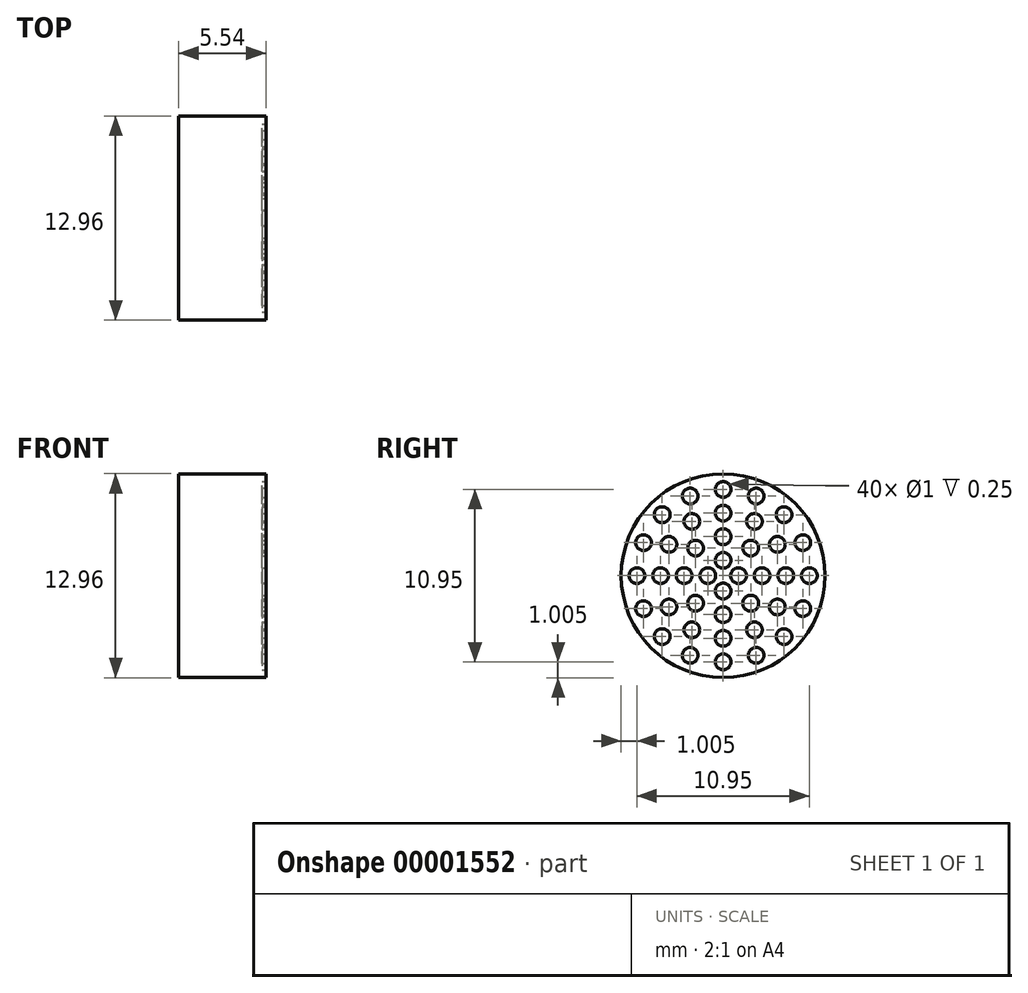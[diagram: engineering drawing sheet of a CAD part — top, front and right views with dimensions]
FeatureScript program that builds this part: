
annotation { "Feature Type Name" : "Feature", "Feature Type Description" : "" }
export const myFeature = defineFeature(function(context is Context, id is Id, definition is map)
    precondition{}
    {
        {
            var Q0;
            Q0=qCreatedBy(makeId("Right.planeOp"),FACE);
            var sketch = newSketch(context, id + "F0", { "sketchPlane" : qUnion([Q0])});
            skCircle(sketch, "E0", {"center": v(0, 0) * mm, "radius": 6.48 * mm});
            skSolve(sketch);
        }
        {
            var Q0;
            Q0 = qSketchRegion(id + "F0", true);
            extrude(context, id + "F1", {"entities" : qUnion([Q0]), "depth" : 5.54 * mm});
        }
        {
            var Q0;
            Q0=makeQuery(id+"F1.opExtrude","CAP_FACE",FACE,{"disambiguationData":[OSD([sQuery(id+"F0.wireOp",EDGE,"E0")])],"isStart":false});
            var sketch = newSketch(context, id + "F2", { "sketchPlane" : qUnion([Q0])});
            skCircle(sketch, "E1", {"center": v(0, 0) * mm, "radius": 5.48 * mm, "construction": true});
            skCircle(sketch, "E2", {"center": v(0, 5.48) * mm, "radius": 0.5 * mm});
            skCircle(sketch, "E3.0", {"center": v(0, 0) * mm, "radius": 3.98 * mm, "construction": true});
            skCircle(sketch, "E4", {"center": v(0, 0) * mm, "radius": 2.48 * mm, "construction": true});
            skCircle(sketch, "E5", {"center": v(0, 0) * mm, "radius": 0.98 * mm, "construction": true});
            skCircle(sketch, "E6", {"center": v(0, 3.98) * mm, "radius": 0.5 * mm});
            skCircle(sketch, "E7", {"center": v(0, 2.48) * mm, "radius": 0.5 * mm});
            skCircle(sketch, "E8", {"center": v(0, 0.98) * mm, "radius": 0.5 * mm});
            skSolve(sketch);
        }
        {
            var Q0;
            Q0=makeQuery(id+"F2.imprint","IMPRINT",FACE,{"disambiguationData":[TD([[makeQuery(id+"F2.imprint","IMPRINT",EDGE,{"derivedFrom":sQuery(id+"F2.wireOp",EDGE,"E2")}),1.0]])]});
            extrude(context, id + "F3", {"entities" : qUnion([Q0]), "operationType" : NewBodyOperationType.REMOVE, "oppositeDirection" : true, "depth" : .25 * mm});
        }
        {
            var Q0;
            Q0=makeQuery(id+"F3.boolean.opBoolean","COPY",FACE,{"derivedFrom":makeQuery(id+"F3.opExtrude","SWEPT_FACE",FACE,{"disambiguationData":[OSD([sQuery(id+"F2.wireOp",EDGE,"E2")])]})});
            var Q1;
            Q1=makeQuery(id+"F3.boolean.opBoolean","COPY",FACE,{"derivedFrom":makeQuery(id+"F3.opExtrude","CAP_FACE",FACE,{"disambiguationData":[OSD([sQuery(id+"F2.wireOp",EDGE,"E2")])],"isStart":false})});
            var Q2;
            Q2=sQuery(id+"F2.wireOp",EDGE,"E1");
            circularPattern(context, id + "F4", {"faces" : qUnion([Q0, Q1]), "axis" : qUnion([Q2]), "angle" : 360 * degree, "instanceCount" : 16, "equalSpace" : true, "patternType" : PatternType.FACE});
        }
        {
            var Q0;
            Q0=makeQuery(id+"F2.imprint","IMPRINT",FACE,{"disambiguationData":[TD([[makeQuery(id+"F2.imprint","IMPRINT",EDGE,{"derivedFrom":sQuery(id+"F2.wireOp",EDGE,"E6")}),1.0]])]});
            var Q1;
            Q1=sQuery(id+"F2.wireOp",EDGE,"E6");
            extrude(context, id + "F5", {"entities" : qUnion([Q0]), "operationType" : NewBodyOperationType.REMOVE, "surfaceEntities" : qUnion([Q1]), "oppositeDirection" : true, "depth" : .25 * mm});
        }
        {
            var Q0;
            Q0=makeQuery(id+"F2.imprint","IMPRINT",FACE,{"disambiguationData":[TD([[makeQuery(id+"F2.imprint","IMPRINT",EDGE,{"derivedFrom":sQuery(id+"F2.wireOp",EDGE,"E7")}),1.0]])]});
            extrude(context, id + "F6", {"entities" : qUnion([Q0]), "operationType" : NewBodyOperationType.REMOVE, "oppositeDirection" : true, "depth" : .25 * mm});
        }
        {
            var Q0;
            Q0=makeQuery(id+"F2.imprint","IMPRINT",FACE,{"disambiguationData":[TD([[makeQuery(id+"F2.imprint","IMPRINT",EDGE,{"derivedFrom":sQuery(id+"F2.wireOp",EDGE,"E8")}),1.0]])]});
            extrude(context, id + "F7", {"entities" : qUnion([Q0]), "operationType" : NewBodyOperationType.REMOVE, "oppositeDirection" : true, "depth" : .25 * mm});
        }
        {
            var Q0;
            Q0=makeQuery(id+"F5.boolean.opBoolean","COPY",FACE,{"derivedFrom":makeQuery(id+"F5.opExtrude","SWEPT_FACE",FACE,{"disambiguationData":[OSD([sQuery(id+"F2.wireOp",EDGE,"E6")])]})});
            var Q1;
            Q1=makeQuery(id+"F5.boolean.opBoolean","COPY",FACE,{"derivedFrom":makeQuery(id+"F5.opExtrude","CAP_FACE",FACE,{"disambiguationData":[OSD([sQuery(id+"F2.wireOp",EDGE,"E6")])],"isStart":false})});
            var Q2;
            Q2=sQuery(id+"F2.wireOp",EDGE,"E3.0");
            circularPattern(context, id + "F8", {"faces" : qUnion([Q0, Q1]), "axis" : qUnion([Q2]), "angle" : 360 * degree, "instanceCount" : 12, "equalSpace" : true, "patternType" : PatternType.FACE});
        }
        {
            var Q0;
            Q0=makeQuery(id+"F6.boolean.opBoolean","COPY",FACE,{"derivedFrom":makeQuery(id+"F6.opExtrude","SWEPT_FACE",FACE,{"disambiguationData":[OSD([sQuery(id+"F2.wireOp",EDGE,"E7")])]})});
            var Q1;
            Q1=makeQuery(id+"F6.boolean.opBoolean","COPY",FACE,{"derivedFrom":makeQuery(id+"F6.opExtrude","CAP_FACE",FACE,{"disambiguationData":[OSD([sQuery(id+"F2.wireOp",EDGE,"E7")])],"isStart":false})});
            var Q2;
            Q2=sQuery(id+"F2.wireOp",EDGE,"E4");
            circularPattern(context, id + "F9", {"faces" : qUnion([Q0, Q1]), "axis" : qUnion([Q2]), "angle" : 360 * degree, "instanceCount" : 8, "equalSpace" : true, "patternType" : PatternType.FACE});
        }
        {
            var Q0;
            Q0=makeQuery(id+"F7.boolean.opBoolean","COPY",FACE,{"derivedFrom":makeQuery(id+"F7.opExtrude","SWEPT_FACE",FACE,{"disambiguationData":[OSD([sQuery(id+"F2.wireOp",EDGE,"E8")])]})});
            var Q1;
            Q1=makeQuery(id+"F7.boolean.opBoolean","COPY",FACE,{"derivedFrom":makeQuery(id+"F7.opExtrude","CAP_FACE",FACE,{"disambiguationData":[OSD([sQuery(id+"F2.wireOp",EDGE,"E8")])],"isStart":false})});
            var Q2;
            Q2=sQuery(id+"F2.wireOp",EDGE,"E5");
            circularPattern(context, id + "F10", {"faces" : qUnion([Q0, Q1]), "axis" : qUnion([Q2]), "angle" : 360 * degree, "instanceCount" : 4, "equalSpace" : true, "patternType" : PatternType.FACE});
        }
    });
